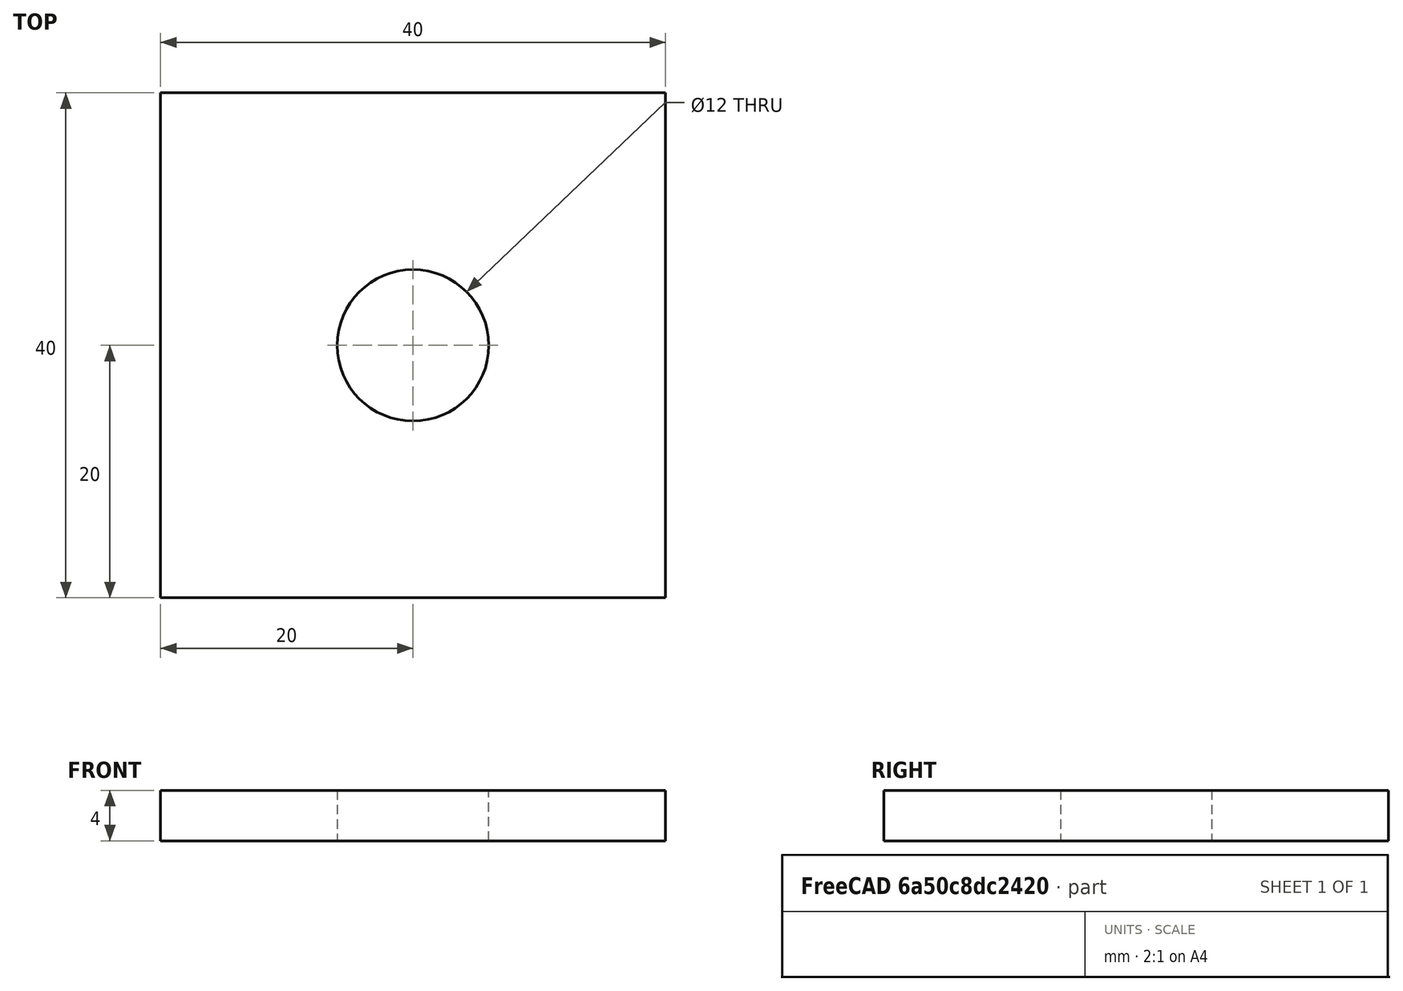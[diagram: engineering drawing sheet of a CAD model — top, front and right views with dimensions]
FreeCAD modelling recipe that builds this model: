
FCSTD DOCUMENT  (FreeCAD 0.20R29410 (Git))
Label: croquis4
License: Creative Commons Attribution-ShareAlike
LicenseURL: http://creativecommons.org/licenses/by-sa/4.0/
objects: Sketcher::SketchObject×1, Part::Extrusion×1
note: 2 computed .brp shape members not serialized (recipe doc carries the construction recipe); baked Part::Feature solids carry a one-line shape summary decoded from their .brp

FEATURE [Sketcher::SketchObject] Sketch
  FullyConstrained = true
  sketch-geometry (5):
    g0: LineSegment StartX=-20 StartY=20 StartZ=0 EndX=20 EndY=20 EndZ=0
    g1: LineSegment StartX=20 StartY=20 StartZ=0 EndX=20 EndY=-20 EndZ=0
    g2: LineSegment StartX=20 StartY=-20 StartZ=0 EndX=-20 EndY=-20 EndZ=0
    g3: LineSegment StartX=-20 StartY=-20 StartZ=0 EndX=-20 EndY=20 EndZ=0
    g4: Circle CenterX=0 CenterY=0 CenterZ=0 NormalX=0 NormalY=0 NormalZ=1 AngleXU=0 Radius=6
  constraints (13):
    c: Coincident(g0,g1)
    c: Coincident(g1,g2)
    c: Coincident(g2,g3)
    c: Coincident(g3,g0)
    c: Horizontal(g0)
    c: Horizontal(g2)
    c: Vertical(g1)
    c: Vertical(g3)
    c: Symmetric(g0,g1,g-1)
    c: Equal(g0,g1)
    c: DistanceX(g0,g0) = 40  'lado'
    c: Coincident(g4,g-1)
    c: Diameter(g4) = 12  'diametro'
FEATURE [Part::Extrusion] Extrude
  Base = -> Sketch
  Dir = (0,0,1)
  DirMode = 2
  FaceMakerClass = Part::FaceMakerBullseye
  LengthFwd = 4
  LengthRev = 0
  Solid = true
  Symmetric = false
